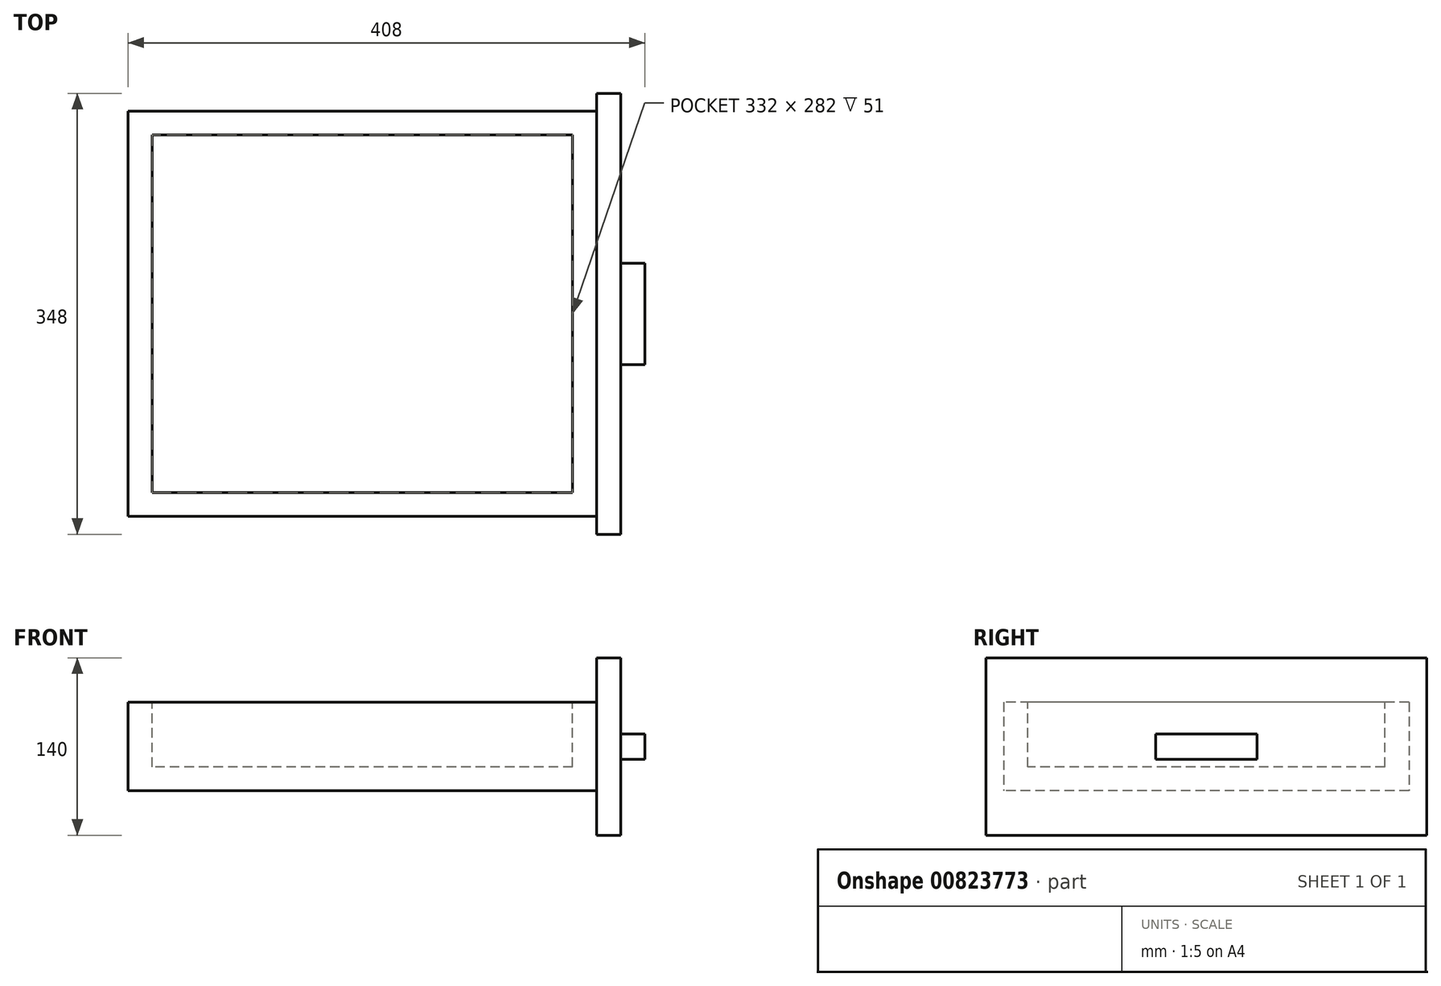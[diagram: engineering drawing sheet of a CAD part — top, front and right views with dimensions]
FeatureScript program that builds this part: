
annotation { "Feature Type Name" : "Feature", "Feature Type Description" : "" }
export const myFeature = defineFeature(function(context is Context, id is Id, definition is map)
    precondition{}
    {
        {
            var Q0;
            Q0=qCreatedBy(makeId("Top.planeOp"),FACE);
            var sketch = newSketch(context, id + "F0", { "sketchPlane" : qUnion([Q0])});
            skLineSegment(sketch, "E0.bottom", {"start": v(185, 160) * mm, "end": v(-185, 160) * mm});
            skLineSegment(sketch, "E0.top", {"start": v(185, -160) * mm, "end": v(-185, -160) * mm});
            skLineSegment(sketch, "E0.left", {"start": v(185, 160) * mm, "end": v(185, -160) * mm});
            skLineSegment(sketch, "E0.right", {"start": v(-185, 160) * mm, "end": v(-185, -160) * mm});
            skPoint(sketch, "E0.middle", {"position": v(0, 0) * mm});
            skSolve(sketch);
        }
        {
            var Q0;
            Q0=makeQuery(id+"F0.imprint","IMPRINT",FACE,{"disambiguationData":[TD([[makeQuery(id+"F0.imprint","IMPRINT",EDGE,{"derivedFrom":sQuery(id+"F0.wireOp",EDGE,"E0.bottom")}),1.0]])]});
            extrude(context, id + "F1", {"entities" : qUnion([Q0]), "depth" : 70 * mm, "offsetDistance" : 25 * mm});
        }
        {
            var Q0;
            Q0=makeQuery(id+"F1.opExtrude","CAP_FACE",FACE,{"disambiguationData":[OSD([sQuery(id+"F0.wireOp",EDGE,"E0.bottom"),sQuery(id+"F0.wireOp",EDGE,"E0.top"),sQuery(id+"F0.wireOp",EDGE,"E0.left"),sQuery(id+"F0.wireOp",EDGE,"E0.right")])],"isStart":false});
            var sketch = newSketch(context, id + "F2", { "sketchPlane" : qUnion([Q0])});
            skLineSegment(sketch, "E1.bottom", {"start": v(166, 141) * mm, "end": v(-166, 141) * mm});
            skLineSegment(sketch, "E1.top", {"start": v(166, -141) * mm, "end": v(-166, -141) * mm});
            skLineSegment(sketch, "E1.left", {"start": v(166, 141) * mm, "end": v(166, -141) * mm});
            skLineSegment(sketch, "E1.right", {"start": v(-166, 141) * mm, "end": v(-166, -141) * mm});
            skPoint(sketch, "E1.middle", {"position": v(0, 0) * mm});
            skSolve(sketch);
        }
        {
            var Q0;
            Q0=makeQuery(id+"F2.imprint","IMPRINT",FACE,{"disambiguationData":[TD([[makeQuery(id+"F2.imprint","IMPRINT",EDGE,{"derivedFrom":sQuery(id+"F2.wireOp",EDGE,"E1.bottom")}),1.0]])]});
            extrude(context, id + "F3", {"entities" : qUnion([Q0]), "operationType" : NewBodyOperationType.REMOVE, "oppositeDirection" : true, "depth" : 51 * mm, "offsetDistance" : 25 * mm});
        }
        {
            var Q0;
            Q0=makeQuery(id+"F1.opExtrude","SWEPT_FACE",FACE,{"disambiguationData":[OSD([sQuery(id+"F0.wireOp",EDGE,"E0.left")])]});
            var sketch = newSketch(context, id + "F4", { "sketchPlane" : qUnion([Q0])});
            skLineSegment(sketch, "E2.bottom", {"start": v(174, 105) * mm, "end": v(-174, 105) * mm});
            skLineSegment(sketch, "E2.top", {"start": v(174, -35) * mm, "end": v(-174, -35) * mm});
            skLineSegment(sketch, "E2.left", {"start": v(174, 105) * mm, "end": v(174, -35) * mm});
            skLineSegment(sketch, "E2.right", {"start": v(-174, 105) * mm, "end": v(-174, -35) * mm});
            skPoint(sketch, "E2.middle", {"position": v(0, 35) * mm});
            skPoint(sketch, "E2.middle.positionSnap0", {"position": v(-160, 35) * mm});
            skPoint(sketch, "E2.middle.positionSnap1", {"position": v(0, 70) * mm});
            skPoint(sketch, "E2.centerSnap0", {"position": v(-160, 35) * mm});
            skPoint(sketch, "E2.centerSnap1", {"position": v(0, 70) * mm});
            skSolve(sketch);
        }
        {
            var Q0;
            Q0=makeQuery(id+"F4.imprint","IMPRINT",FACE,{"disambiguationData":[TD([[makeQuery(id+"F4.imprint","IMPRINT",EDGE,{"derivedFrom":sQuery(id+"F4.wireOp",EDGE,"E2.bottom")}),1.0]])]});
            var Q1;
            {var subQ0=sQuery(id+"F0.wireOp",EDGE,"E0.left");Q1=makeQuery(id+"F4.imprint","IMPRINT",FACE,{"disambiguationData":[TD([[makeQuery(id+"F4.imprint","IMPRINT",EDGE,{"derivedFrom":makeQuery(id+"F1.opExtrude","CAP_EDGE",EDGE,{"disambiguationData":[OSD([subQ0])],"isStart":true})}),-1.0]])]});}
            extrude(context, id + "F5", {"entities" : qUnion([Q0, Q1]), "operationType" : NewBodyOperationType.ADD, "depth" : 19 * mm, "offsetDistance" : 25 * mm});
        }
        {
            var Q0;
            Q0=makeQuery(id+"F5.opExtrude","CAP_FACE",FACE,{"disambiguationData":[OSD([sQuery(id+"F4.wireOp",EDGE,"E2.bottom"),sQuery(id+"F4.wireOp",EDGE,"E2.top"),sQuery(id+"F4.wireOp",EDGE,"E2.left"),sQuery(id+"F4.wireOp",EDGE,"E2.right")])],"isStart":false});
            var sketch = newSketch(context, id + "F6", { "sketchPlane" : qUnion([Q0])});
            skLineSegment(sketch, "E3.bottom", {"start": v(40, 45) * mm, "end": v(-40, 45) * mm});
            skLineSegment(sketch, "E3.top", {"start": v(40, 25) * mm, "end": v(-40, 25) * mm});
            skLineSegment(sketch, "E3.left", {"start": v(40, 45) * mm, "end": v(40, 25) * mm});
            skLineSegment(sketch, "E3.right", {"start": v(-40, 45) * mm, "end": v(-40, 25) * mm});
            skPoint(sketch, "E3.middle", {"position": v(0, 35) * mm});
            skPoint(sketch, "E3.middle.positionSnap0", {"position": v(-174, 35) * mm});
            skPoint(sketch, "E3.centerSnap0", {"position": v(-174, 35) * mm});
            skSolve(sketch);
        }
        {
            var Q0;
            Q0=makeQuery(id+"F6.imprint","IMPRINT",FACE,{"disambiguationData":[TD([[makeQuery(id+"F6.imprint","IMPRINT",EDGE,{"derivedFrom":sQuery(id+"F6.wireOp",EDGE,"E3.bottom")}),1.0]])]});
            extrude(context, id + "F7", {"entities" : qUnion([Q0]), "operationType" : NewBodyOperationType.ADD, "depth" : 19 * mm, "offsetDistance" : 25 * mm});
        }
    });
